# Revit family: PLASTIC CHANNEL BASE DN100 Grate vertical outlet
name_source: partatom
category: Оборудование
units: mm (PartAtom-declared; Revit-internal decimal feet)

## family parameters
Общий = Да
Основа = Грань
При загрузке вырезать с полостями = Нет
Размер круглого соединителя = Использовать диаметр
Тип детали = Нормальный
Точка расчета площади = Нет

## types (38) — shared parameters
A10-01 = Stainless Steel Mesh ADA B125 : 20502
A10-02 = Stainless Steel Heelproof A15 : 205018
A10-03 = Stainless Steel Heelproof A15 screw fastening : 2050181
A10-04 = Stainless Steel Mesh A15 : 205016
A10-05 = Stainless Steel Mesh ADA A15 : 2050
A10-06 = Stainless steel slotted A15 : 2090
A10-07 = Stainless steel slotted for fastener A15 : 20901
A10-08 = Brass slotted A15 : 2070
A10-09 = Brass slotted for fastener A15 : 20701
A10-10 = Copper slotted A15 : 2060
A10-11 = Copper slotted for fastener A15 : 20601
A10-12 = Galvanized Steel Mesh ADA B125 : 20202
A10-13 = Galvanized Steel Heelproof A15 : 202018
A10-14 = Galvanized Steel Heelproof A15 screw fastening : 2020181
A10-15 = Galvanized Steel Mesh A15 : 202016
A10-16 = Galvanized Steel Mesh ADA A15 : 2020
A10-17 = Galvanized steel slotted A15 : 2010
A10-18 = Galvanized steel slotted for fastener A15 : 20101
A5-01 = Cast iron mesh В125 : 20402
A5-02 = Cast iron slotted ADA С250 : 20403-ADA
A5-03 = Cast iron slotted С250 : 283031
A5-04 = Cast iron slotted anti-slip С250 : 20303
A5-05 = Cast iron slotted Protector С250 : 203032
A5-06 = Cast iron slotted Wave С250 : 2030351
A5-07 = Plastic slotted A15 : 208019
ADSK_Dimension_Diameter = 100 мм
ADSK_Dimension_Lenght = 1000 мм
ADSK_Dimension_Width = 160 мм
ADSK_Load class = C250
ADSK_Manufacturer = Vodaland
ADSK_Material_Name = Plastic
ADSK_Unit = pcs
Cap1 = Plastic end cap Base DN100 : 630-1
Cap2 = Plastic end cap Base DN100 : 630-2
Cap3 = Plastic end cap Base DN100 : 630-3
Cap8010 = Plastic end cap Base DN100 : 630080
Cap8020 = Plastic end cap Base DN100 : 630120
Cap8050 = Plastic end cap Base DN100 : 630060
Connection on the left = TC : Left
Connection on the right = TC : Right
Fa1 = Choice of fastening : 6100-35
Fa2 = Choice of fastening : 6200-35
Fr1 = Fastening : 6100-35
Fr2 = Fastening : 6200-35
Fr3 = Fastening : 6800-35
G10-01 = Stainless Steel Grate Base DN100 Mesh ADA B125 : 20502
G10-02 = Stainless Steel Grate Base DN100 Heelproof A15 : 205018
G10-03 = Stainless Steel Grate Base DN100 Heelproof A15 screw fastening : 2050181
G10-04 = Stainless Steel Grate Base DN100 Mesh A15 : 205016
G10-05 = Stainless Steel Grate Base DN100 Mesh ADA A15 : 2050
G10-06 = Stainless steel grate Base DN100 slotted A15 : 2090
G10-07 = Stainless steel grate Base DN100 slotted for fastener A15 : 20901
G10-08 = Brass grate Base DN100 slotted A15 : 2070
G10-09 = Brass grate Base DN100 slotted for fastener A15 : 20701
G10-10 = Copper grate Base DN100 slotted A15 : 2060
G10-11 = Copper grate Base DN100 slotted for fastener A15 : 20601
G10-12 = Galvanized Steel Grate Base DN100 Mesh ADA B125 : 20202
G10-13 = Galvanized Steel Grate Base DN100 Heelproof A15 : 202018
G10-14 = Galvanized Steel Grate Base DN100 Heelproof A15 screw fastening : 2020181
G10-15 = Galvanized Steel Grate Base DN100 Mesh A15 : 202016
G10-16 = Galvanized Steel Grate Base DN100 Mesh ADA A15 : 2020
G10-17 = Galvanized steel grate Base DN100 slotted A15 : 2010
G10-18 = Galvanized steel grate Base DN100 slotted for fastener A15 : 20101
G5-01 = Cast iron grate Base DN100 mesh В125 : 20402
G5-02 = Cast iron grate Base DN100 slotted ADA С250 : 20403-ADA
G5-03 = Cast iron grate Base DN100 slotted С250 : 283031
G5-04 = Cast iron grate Base DN100 slotted anti-slip С250 : 20303
G5-05 = Cast iron grate Base DN100 slotted Protector С250 : 203032
G5-06 = Cast iron grate Base DN100 slotted Wave С250 : 2030351
G5-07 = Plastic grate Base DN100 slotted A15 : 208019
W1 = 160 мм
W2 = 156 мм
bias = Нет
no = No
Группа модели = Linear drainage
zero-valued in all types: Отметка по умолчанию

## per-type parameters (varying)
| type | ADSK_Dimension_Height | ADSK_Name | ADSK_Sealant | ADSK_Weight | CN | Cap_begin | Cap_end | H1 | H2 | R1 | R2 |
| 80060 | 60 мм | Plastic channel Base DN100 H60 | 10 | 1.2 | 8050 | Plastic end cap Base DN100 : 630060 | Plastic end cap Base DN100 : 630060 | 20 мм | 20 мм | 5 мм | 5 мм |
| 80080-1 | 80 мм | Plastic slope channel Base DN100 H80 1 | 11 | 1.4 | 80080 | Plastic end cap Base DN100 : 630060 | Plastic end cap Base DN100 : 630-1 | 40 мм | 40 мм | 5 мм | 25 мм |
| 80080 | 80 мм | Plastic channel Base DN100 H80 | 11 | 1.2 | 8010 | Plastic end cap Base DN100 : 630080 | Plastic end cap Base DN100 : 630080 | 40 мм | 40 мм | 25 мм | 25 мм |
| 80090-2 | 90 мм | Plastic slope channel Base DN100 H90 2 | 11 | 1.4 | 80090 | Plastic end cap Base DN100 : 630-1 | Plastic end cap Base DN100 : 630-1 | 50 мм | 50 мм | 25 мм | 25 мм |
| 80100-3 | 100 мм | Plastic slope channel Base DN100 H100 3 | 12 | 1.5 | 80100 | Plastic end cap Base DN100 : 630-1 | Plastic end cap Base DN100 : 630-2 | 60 мм | 60 мм | 25 мм | 49 мм |
| 80100 | 100 мм | Plastic channel Base DN100 H100 | 12 | 1.4 | 80100 | Plastic end cap Base DN100 : 630-1 | Plastic end cap Base DN100 : 630-2 | 60 мм | 60 мм | 49 мм | 49 мм |
| 80110-4 | 110 мм | Plastic slope channel Base DN100 H110 4 | 12 | 1.7 | 80110 | Plastic end cap Base DN100 : 630-2 | Plastic end cap Base DN100 : 630-2 | 70 мм | 70 мм | 49 мм | 49 мм |
| 80120-5 | 120 мм | Plastic slope channel Base DN100 H120 5 | 13 | 1.8 | 80120 | Plastic end cap Base DN100 : 630-2 | Plastic end cap Base DN100 : 630-2 | 80 мм | 80 мм | 49 мм | 49 мм |
| 80120 | 120 мм | Plastic channel Base DN100 H120 | 13 | 1.8 | 8020 | Plastic end cap Base DN100 : 630120 | Plastic end cap Base DN100 : 630120 | 80 мм | 80 мм | 49 мм | 49 мм |
| 80130-6 | 130 мм | Plastic slope channel Base DN100 H130 6 | 14 | 1.8 | 80130 | Plastic end cap Base DN100 : 630-2 | Plastic end cap Base DN100 : 630-2 | 90 мм | 90 мм | 49 мм | 49 мм |
| 80140-7 | 140 мм | Plastic slope channel Base DN100 H140 7 | 14 | 1.9 | 80140 | Plastic end cap Base DN100 : 630-2 | Plastic end cap Base DN100 : 630-2 | 100 мм | 100 мм | 49 мм | 49 мм |
| 80150-8 | 150 мм | Plastic slope channel Base DN100 H150 8 | 16 | 2 | 80150 | Plastic end cap Base DN100 : 630-2 | Plastic end cap Base DN100 : 630-2 | 110 мм | 110 мм | 49 мм | 49 мм |
| 80150 | 150 мм | Plastic channel Base DN100 H150 | 16 | 2.1 | 8000 | Plastic end cap Base DN100 : 630-2 | Plastic end cap Base DN100 : 630-2 | 110 мм | 110 мм | 49 мм | 49 мм |
| 80160-9 | 160 мм | Plastic slope channel Base DN100 H160 9 | 17 | 2.1 | 80160 | Plastic end cap Base DN100 : 630-2 | Plastic end cap Base DN100 : 630-3 | 120 мм | 120 мм | 49 мм | 49 мм |
| 80170-10 | 170 мм | Plastic slope channel Base DN100 H170 10 | 18 | 2.2 | 80170 | Plastic end cap Base DN100 : 630-3 | Plastic end cap Base DN100 : 630-3 | 130 мм | 130 мм | 49 мм | 49 мм |
| 80180-11 | 180 мм | Plastic slope channel Base DN100 H180 11 | 19 | 2.3 | 80180 | Plastic end cap Base DN100 : 630-3 | Plastic end cap Base DN100 : 630-3 | 140 мм | 140 мм | 49 мм | 49 мм |
| 80190-12 | 190 мм | Plastic slope channel Base DN100 H190 12 | 20 | 2.4 | 80190 | Plastic end cap Base DN100 : 630-3 | Plastic end cap Base DN100 : 630-3 | 150 мм | 150 мм | 49 мм | 49 мм |
| 80200-13 | 200 мм | Plastic slope channel Base DN100 H200 13 | 21 | 2.5 | 80200 | Plastic end cap Base DN100 : 630-3 | Plastic end cap Base DN100 : 630-3 | 160 мм | 160 мм | 49 мм | 49 мм |
| 80200 | 200 мм | Plastic channel Base DN100 H200 | 21 | 2.5 | 80200 | Plastic end cap Base DN100 : 630-3 | Plastic end cap Base DN100 : 630-3 | 160 мм | 160 мм | 49 мм | 49 мм |
| 80067 | 60 мм | Plastic channel Base DN100 H60 reinforced | 10 | 1.2 | 8050 | Plastic end cap Base DN100 : 630060 | Plastic end cap Base DN100 : 630060 | 20 мм | 20 мм | 5 мм | 5 мм |
| 80087-1 | 80 мм | Plastic slope channel Base DN100 H80 1 reinforced | 11 | 1.4 | 80080 | Plastic end cap Base DN100 : 630060 | Plastic end cap Base DN100 : 630-1 | 40 мм | 40 мм | 5 мм | 25 мм |
| 80087 | 80 мм | Plastic channel Base DN100 H80 reinforced | 11 | 1.2 | 8010 | Plastic end cap Base DN100 : 630080 | Plastic end cap Base DN100 : 630080 | 40 мм | 40 мм | 25 мм | 25 мм |
| 80097-2 | 90 мм | Plastic slope channel Base DN100 H90 2 reinforced | 11 | 1.4 | 80090 | Plastic end cap Base DN100 : 630-1 | Plastic end cap Base DN100 : 630-1 | 50 мм | 50 мм | 25 мм | 25 мм |
| 80107-3 | 100 мм | Plastic slope channel Base DN100 H100 3 reinforced | 12 | 1.5 | 80100 | Plastic end cap Base DN100 : 630-1 | Plastic end cap Base DN100 : 630-2 | 60 мм | 60 мм | 25 мм | 49 мм |
| 80107 | 100 мм | Plastic channel Base DN100 H100 reinforced | 12 | 1.4 | 80100 | Plastic end cap Base DN100 : 630-1 | Plastic end cap Base DN100 : 630-2 | 60 мм | 60 мм | 49 мм | 49 мм |
| 80117-4 | 110 мм | Plastic slope channel Base DN100 H110 4 reinforced | 12 | 1.7 | 80110 | Plastic end cap Base DN100 : 630-2 | Plastic end cap Base DN100 : 630-2 | 70 мм | 70 мм | 49 мм | 49 мм |
| 80127-5 | 120 мм | Plastic slope channel Base DN100 H120 5 reinforced | 13 | 1.8 | 80120 | Plastic end cap Base DN100 : 630-2 | Plastic end cap Base DN100 : 630-2 | 80 мм | 80 мм | 49 мм | 49 мм |
| 80127 | 120 мм | Plastic channel Base DN100 H120 reinforced | 13 | 1.8 | 8020 | Plastic end cap Base DN100 : 630120 | Plastic end cap Base DN100 : 630120 | 80 мм | 80 мм | 49 мм | 49 мм |
| 80137-6 | 130 мм | Plastic slope channel Base DN100 H130 6 reinforced | 14 | 1.8 | 80130 | Plastic end cap Base DN100 : 630-2 | Plastic end cap Base DN100 : 630-2 | 90 мм | 90 мм | 49 мм | 49 мм |
| 80147-7 | 140 мм | Plastic slope channel Base DN100 H140 7 reinforced | 14 | 1.9 | 80140 | Plastic end cap Base DN100 : 630-2 | Plastic end cap Base DN100 : 630-2 | 100 мм | 100 мм | 49 мм | 49 мм |
| 80157-8 | 150 мм | Plastic slope channel Base DN100 H150 8 reinforced | 16 | 2 | 80150 | Plastic end cap Base DN100 : 630-2 | Plastic end cap Base DN100 : 630-2 | 110 мм | 110 мм | 49 мм | 49 мм |
| 80157 | 150 мм | Plastic channel Base DN100 H150 reinforced | 16 | 2.1 | 8000 | Plastic end cap Base DN100 : 630-2 | Plastic end cap Base DN100 : 630-2 | 110 мм | 110 мм | 49 мм | 49 мм |
| 80167-9 | 160 мм | Plastic slope channel Base DN100 H160 9 reinforced | 17 | 2.1 | 80160 | Plastic end cap Base DN100 : 630-2 | Plastic end cap Base DN100 : 630-3 | 120 мм | 120 мм | 49 мм | 49 мм |
| 80177-10 | 170 мм | Plastic slope channel Base DN100 H170 10 reinforced | 18 | 2.2 | 80170 | Plastic end cap Base DN100 : 630-3 | Plastic end cap Base DN100 : 630-3 | 130 мм | 130 мм | 49 мм | 49 мм |
| 80187-11 | 180 мм | Plastic slope channel Base DN100 H180 11 reinforced | 19 | 2.3 | 80180 | Plastic end cap Base DN100 : 630-3 | Plastic end cap Base DN100 : 630-3 | 140 мм | 140 мм | 49 мм | 49 мм |
| 80197-12 | 190 мм | Plastic slope channel Base DN100 H190 12 reinforced | 20 | 2.4 | 80190 | Plastic end cap Base DN100 : 630-3 | Plastic end cap Base DN100 : 630-3 | 150 мм | 150 мм | 49 мм | 49 мм |
| 80207-13 | 200 мм | Plastic slope channel Base DN100 H200 13 reinforced | 21 | 2.5 | 80200 | Plastic end cap Base DN100 : 630-3 | Plastic end cap Base DN100 : 630-3 | 160 мм | 160 мм | 49 мм | 49 мм |
| 80207 | 200 мм | Plastic channel Base DN100 H200 reinforced | 21 | 2.5 | 80200 | Plastic end cap Base DN100 : 630-3 | Plastic end cap Base DN100 : 630-3 | 160 мм | 160 мм | 49 мм | 49 мм |

note: column(s) folded — value = type name in every type: ADSK_Product code

## geometry (parser evidence)
native form markers: Blend x16
no freeform markers — native parametric forms only
